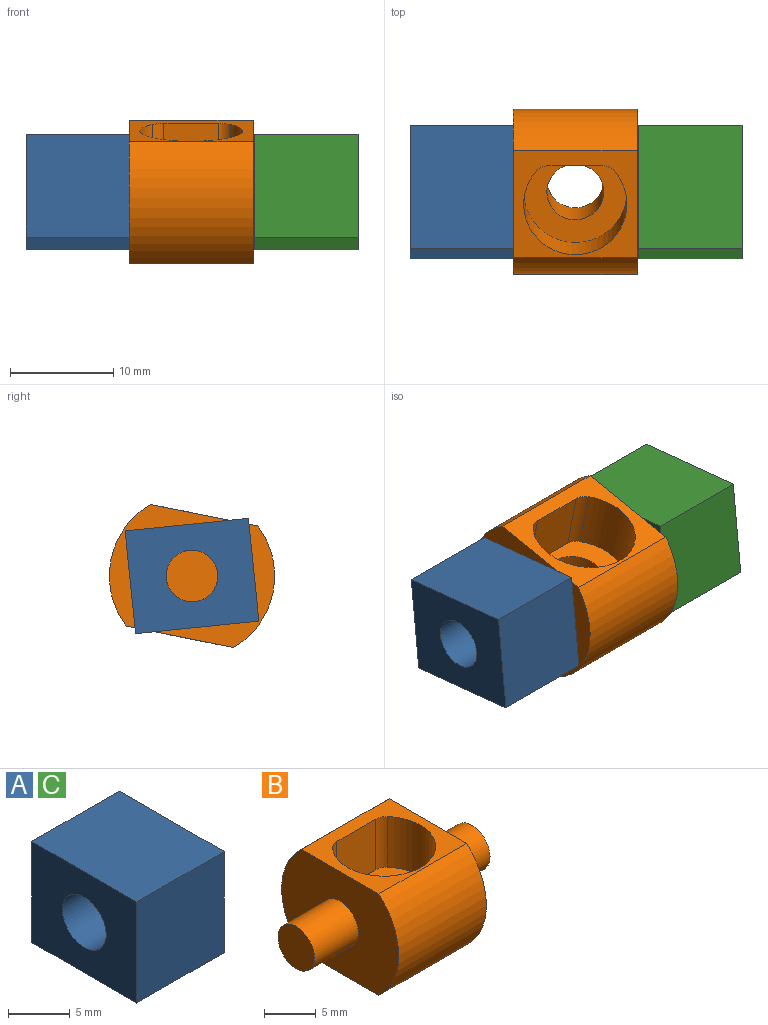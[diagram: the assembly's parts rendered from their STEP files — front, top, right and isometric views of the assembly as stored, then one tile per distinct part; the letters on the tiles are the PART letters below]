
ASSEMBLY  parts=3 mates=5
PART A: 7 faces, bbox 10x12x10 mm
  f0: plane 12x10mm, normal (0,0,1), area 120mm2, adj f1,f4,f5,f6
  f1: plane 10x10mm, normal (0,-1,0), area 100mm2, adj f0,f2,f5,f6
  f2: plane 12x10mm, normal (0,0,-1), area 120mm2, adj f1,f4,f5,f6
  f3: cylinder r=2.5mm len=10mm, axis (-1,0,0), area 157.1mm2, adj f5,f6
  f4: plane 10x10mm, normal (0,1,0), area 100mm2, adj f0,f2,f5,f6
  f5: plane 12x10mm, normal (1,0,0), area 100.4mm2, adj f0,f1,f2,f3,f4
  f6: plane 12x10mm, normal (-1,0,0), area 100.4mm2, adj f0,f1,f2,f3,f4
PART B: 16 faces, bbox 24x16x12 mm
  f0: cylinder r=5mm len=10mm, axis (0,0,1), area 137.1mm2, adj f1,f2,f14,f15
  f1: plane 10x8.79mm, normal (0,0,1), area 49.3mm2, adj f0,f12,f13,f14,f15
  f2: plane 12x10.58mm, normal (0,0,1), area 54mm2, adj f0,f3,f5,f6,f7,f13,f14,f15
  f3: cylinder r=8mm len=12mm, axis (-1,0,0), area 162.8mm2, adj f2,f4,f6,f7
  f4: plane 12x10.58mm, normal (0,0,-1), area 103.2mm2, adj f3,f5,f6,f7,f12
  f5: cylinder r=8mm len=12mm, axis (-1,0,0), area 162.8mm2, adj f2,f4,f6,f7
  f6: plane 16x12mm, normal (1,0,0), area 152.4mm2, adj f2,f3,f4,f5,f10
  f7: plane 16x12mm, normal (-1,0,0), area 152.4mm2, adj f2,f3,f4,f5,f9
  f8: plane 5x5mm, normal (-1,0,0), area 19.6mm2, adj f9
  f9: cylinder r=2.5mm len=6mm, axis (-1,0,0), area 94.2mm2, adj f7,f8
  f10: cylinder r=2.5mm len=6mm, axis (-1,0,0), area 94.2mm2, adj f6,f11
  f11: plane 5x5mm, normal (1,0,0), area 19.6mm2, adj f10
  f12: cylinder r=2.75mm len=6mm, axis (0,0,1), area 103.7mm2, adj f1,f4
  f13: plane 6x5.29mm, normal (0,-1,0), area 31.7mm2, adj f1,f2,f14,f15
  f14: cylinder r=1.5mm len=6mm, axis (0,0,1), area 7.7mm2, adj f0,f1,f2,f13
  f15: cylinder r=1.5mm len=6mm, axis (0,0,1), area 7.7mm2, adj f0,f1,f2,f13
PART C: same geometry as A
PLACE A rot(axis=(-1,0,0),5.8deg) t=(-16,0.05,-0.23)mm
PLACE B rot(axis=(1,0,0),11.3deg) t=(0,0.05,-0.23)mm fixed
PLACE C rot(axis=(-1,0,0),5.8deg) t=(6.14,0.05,-0.23)mm
MATE parallel A.f3 <-> B.f9  axis (1,0,0) through (-6,0.05,-0.23)mm
MATE cylindrical B.f9 <-> C.f3  axis (-1,0,0) through (9,0.05,-0.23)mm
MATE planar C.f0 <-> A.f0  axis (0,0.1,0.99) through (11.14,0.56,4.75)mm
MATE parallel C.f3 <-> B.f6  axis (-1,0,0) through (6.14,0.05,-0.23)mm
MATE cylindrical B.f9 <-> A.f3  axis (-1,0,0) through (-6,0.05,-0.23)mm
